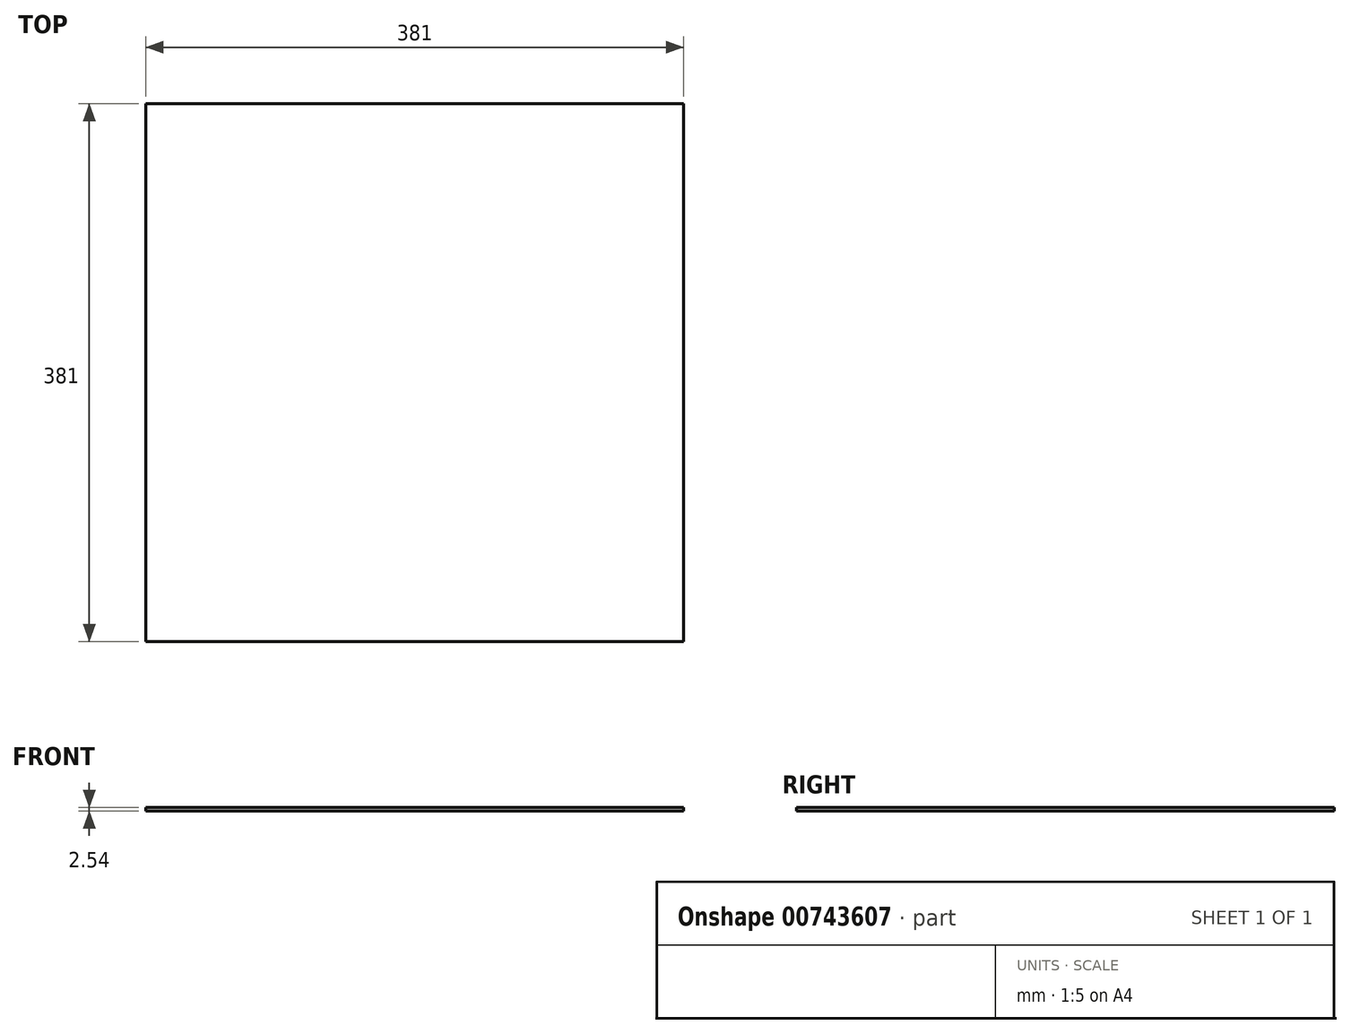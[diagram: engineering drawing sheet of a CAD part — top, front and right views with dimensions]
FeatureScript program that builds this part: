
annotation { "Feature Type Name" : "Feature", "Feature Type Description" : "" }
export const myFeature = defineFeature(function(context is Context, id is Id, definition is map)
    precondition{}
    {
        {
            var Q0;
            Q0=qCreatedBy(makeId("Top.planeOp"),FACE);
            var sketch = newSketch(context, id + "F0", { "sketchPlane" : qUnion([Q0])});
            skLineSegment(sketch, "E0.bottom", {"start": v(190.5, -190.5) * mm, "end": v(-190.5, -190.5) * mm});
            skLineSegment(sketch, "E0.top", {"start": v(190.5, 190.5) * mm, "end": v(-190.5, 190.5) * mm});
            skLineSegment(sketch, "E0.left", {"start": v(190.5, -190.5) * mm, "end": v(190.5, 190.5) * mm});
            skLineSegment(sketch, "E0.right", {"start": v(-190.5, -190.5) * mm, "end": v(-190.5, 190.5) * mm});
            skPoint(sketch, "E0.middle", {"position": v(0, 0) * mm});
            skSolve(sketch);
        }
        {
            var Q0;
            Q0 = qSketchRegion(id + "F0", true);
            extrude(context, id + "F1", {"entities" : qUnion([Q0]), "depth" : 2.54 * mm, "offsetDistance" : 25.4 * mm});
        }
    });
